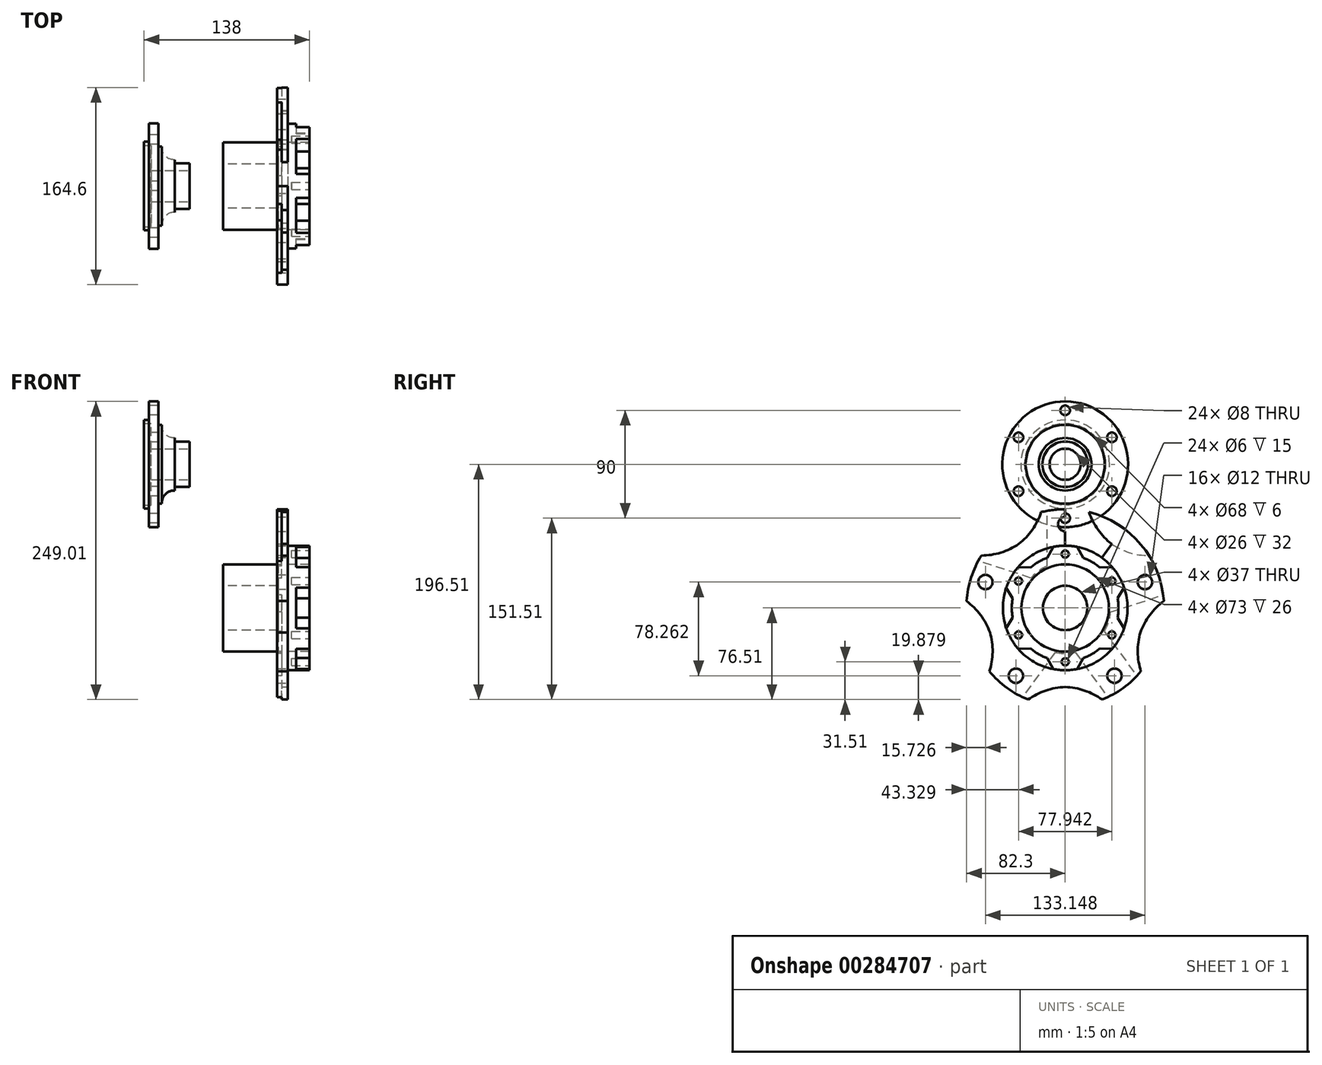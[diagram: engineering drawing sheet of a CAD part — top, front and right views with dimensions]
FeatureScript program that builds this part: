
annotation { "Feature Type Name" : "Feature", "Feature Type Description" : "" }
export const myFeature = defineFeature(function(context is Context, id is Id, definition is map)
    precondition{}
    {
        {
            var Q0;
            Q0=qCreatedBy(makeId("Front.planeOp"),FACE);
            var sketch = newSketch(context, id + "F0", { "sketchPlane" : qUnion([Q0])});
            skPoint(sketch, "E0", {"position": v(0, 13) * mm});
            skPoint(sketch, "E1", {"position": v(0, 19) * mm});
            skLineSegment(sketch, "E2", {"start": v(0, 19) * mm, "end": v(0, 13) * mm});
            skLineSegment(sketch, "E3", {"start": v(0, 19) * mm, "end": v(-12.5, 19) * mm});
            skLineSegment(sketch, "E4", {"start": v(-12.5, 19) * mm, "end": v(-12.5, 22) * mm});
            skLineSegment(sketch, "E5", {"start": v(0, 0) * mm, "end": v(-38, 0) * mm, "construction": true});
            skLineSegment(sketch, "E6", {"start": v(-38, 0) * mm, "end": v(-38, 37) * mm});
            skLineSegment(sketch, "E7", {"start": v(-38, 37) * mm, "end": v(-34, 37) * mm});
            skLineSegment(sketch, "E8", {"start": v(-34, 37) * mm, "end": v(-34, 52.5) * mm});
            skLineSegment(sketch, "E9", {"start": v(-34, 52.5) * mm, "end": v(-26, 52.5) * mm});
            skLineSegment(sketch, "E10", {"start": v(-26, 52.5) * mm, "end": v(-26, 33) * mm});
            skLineSegment(sketch, "E11", {"start": v(-26, 33) * mm, "end": v(-23, 33) * mm});
            skLineSegment(sketch, "E12", {"start": v(-23, 33) * mm, "end": v(-12.5, 33) * mm, "construction": true});
            skLineSegment(sketch, "E13", {"start": v(-12.5, 33) * mm, "end": v(-12.5, 22) * mm, "construction": true});
            skArc(sketch, "E14", {"start": v(-23, 33) * mm, "mid": v(-20.29, 25.08) * mm, "end": v(-12.5, 22) * mm});
            skLineSegment(sketch, "E15", {"start": v(-34, 37) * mm, "end": v(-32, 37) * mm});
            skLineSegment(sketch, "E16", {"start": v(-32, 37) * mm, "end": v(-32, 34) * mm});
            skLineSegment(sketch, "E17", {"start": v(-32, 34) * mm, "end": v(-38, 34) * mm});
            skLineSegment(sketch, "E18", {"start": v(-32, 34) * mm, "end": v(-32, 13) * mm});
            skLineSegment(sketch, "E19", {"start": v(-32, 13) * mm, "end": v(0, 13) * mm});
            skSolve(sketch);
        }
        {
            var Q0;
            Q0=qSketchRegion(id+"F0",true);
            var Q1;
            Q1=sQuery(id+"F0.wireOp",EDGE,"E5");
            revolve(context, id + "F1", {"entities" : qUnion([Q0]), "axis" : qUnion([Q1]), "revolveType" : RevolveType.FULL});
        }
        {
            var Q0;
            Q0=makeQuery(id+"F1.opRevolve","SWEPT_FACE",FACE,{"disambiguationData":[OSD([sQuery(id+"F0.wireOp",EDGE,"E8")])]});
            var sketch = newSketch(context, id + "F2", { "sketchPlane" : qUnion([Q0])});
            skPoint(sketch, "E20", {"position": v(0, 45) * mm});
            skCircle(sketch, "E21", {"center": v(0, 45) * mm, "radius": 4 * mm});
            skCircle(sketch, "E22.1.0", {"center": v(-38.97, 22.5) * mm, "radius": 4 * mm});
            skCircle(sketch, "E22.2.0", {"center": v(-38.97, -22.5) * mm, "radius": 4 * mm});
            skCircle(sketch, "E22.3.0", {"center": v(0, -45) * mm, "radius": 4 * mm});
            skCircle(sketch, "E22.4.0", {"center": v(38.97, -22.5) * mm, "radius": 4 * mm});
            skCircle(sketch, "E22.5.0", {"center": v(38.97, 22.5) * mm, "radius": 4 * mm});
            skPoint(sketch, "E22.center", {"position": v(0, 0) * mm});
            skSolve(sketch);
        }
        {
            var Q0;
            Q0=qSketchRegion(id+"F2",true);
            extrude(context, id + "F3", {"entities" : qUnion([Q0]), "operationType" : NewBodyOperationType.REMOVE, "oppositeDirection" : true, "depth" : 8 * mm});
        }
        {
            var Q0;
            Q0=qCreatedBy(makeId("Front.planeOp"),FACE);
            var sketch = newSketch(context, id + "F4", { "sketchPlane" : qUnion([Q0])});
            skPoint(sketch, "E23", {"position": v(0, 0) * mm});
            skPoint(sketch, "E24", {"position": v(0, -120) * mm});
            skLineSegment(sketch, "E25", {"start": v(0, -120) * mm, "end": v(100, -120) * mm, "construction": true});
            skLineSegment(sketch, "E26", {"start": v(100, -120) * mm, "end": v(100, -68) * mm, "construction": true});
            skLineSegment(sketch, "E27", {"start": v(100, -68) * mm, "end": v(82, -68) * mm});
            skLineSegment(sketch, "E28", {"start": v(82, -68) * mm, "end": v(82, -37.5) * mm});
            skLineSegment(sketch, "E29", {"start": v(82, -37.5) * mm, "end": v(73, -37.5) * mm});
            skLineSegment(sketch, "E30", {"start": v(73, -37.5) * mm, "end": v(73, -83.5) * mm});
            skLineSegment(sketch, "E31", {"start": v(73, -83.5) * mm, "end": v(28, -83.5) * mm});
            skLineSegment(sketch, "E32", {"start": v(28, -83.5) * mm, "end": v(28, -101.5) * mm});
            skLineSegment(sketch, "E33", {"start": v(28, -101.5) * mm, "end": v(73, -101.5) * mm});
            skLineSegment(sketch, "E34", {"start": v(100, -68) * mm, "end": v(100, -83.5) * mm});
            skLineSegment(sketch, "E35", {"start": v(100, -83.5) * mm, "end": v(73, -83.5) * mm});
            skLineSegment(sketch, "E36", {"start": v(73, -83.5) * mm, "end": v(73, -101.5) * mm});
            skPoint(sketch, "E37", {"position": v(73, -37.5) * mm});
            skLineSegment(sketch, "E38", {"start": v(73, -83.5) * mm, "end": v(74, -83.5) * mm});
            skLineSegment(sketch, "E39", {"start": v(74, -83.5) * mm, "end": v(74, -101.5) * mm});
            skLineSegment(sketch, "E40", {"start": v(74, -101.5) * mm, "end": v(73, -101.5) * mm});
            skSolve(sketch);
        }
        {
            var Q0;
            Q0=qSketchRegion(id+"F4",true);
            var Q1;
            Q1=makeQuery(id+"F4.imprint","IMPRINT",FACE,{"disambiguationData":[TD([[makeQuery(id+"F4.imprint","IMPRINT",EDGE,{"derivedFrom":sQuery(id+"F4.wireOp",EDGE,"E36")}),1.0]])]});
            var Q2;
            Q2=sQuery(id+"F4.wireOp",EDGE,"E25");
            revolve(context, id + "F5", {"entities" : qUnion([Q0, Q1]), "axis" : qUnion([Q2]), "revolveType" : RevolveType.FULL});
        }
        {
            var Q0;
            Q0=makeQuery(id+"F5.opRevolve","SWEPT_FACE",FACE,{"disambiguationData":[OSD([sQuery(id+"F4.wireOp",EDGE,"E28")])]});
            var sketch = newSketch(context, id + "F6", { "sketchPlane" : qUnion([Q0])});
            skCircle(sketch, "E41.0", {"center": v(0, -120) * mm, "radius": 82.5 * mm});
            skPoint(sketch, "E42", {"position": v(0, -50) * mm});
            skCircle(sketch, "E43", {"center": v(0, -50) * mm, "radius": 6 * mm});
            skCircle(sketch, "E44.1.0", {"center": v(-66.57, -98.37) * mm, "radius": 6 * mm});
            skCircle(sketch, "E44.2.0", {"center": v(-41.14, -176.63) * mm, "radius": 6 * mm});
            skCircle(sketch, "E44.3.0", {"center": v(41.14, -176.63) * mm, "radius": 6 * mm});
            skCircle(sketch, "E44.4.0", {"center": v(66.57, -98.37) * mm, "radius": 6 * mm});
            skSolve(sketch);
        }
        {
            var Q0;
            Q0=makeQuery(id+"F6.imprint","IMPRINT",FACE,{"disambiguationData":[TD([[makeQuery(id+"F6.imprint","IMPRINT",EDGE,{"derivedFrom":sQuery(id+"F6.wireOp",EDGE,"E43")}),1.0]])]});
            var Q1;
            Q1=makeQuery(id+"F6.imprint","IMPRINT",FACE,{"disambiguationData":[TD([[makeQuery(id+"F6.imprint","IMPRINT",EDGE,{"derivedFrom":sQuery(id+"F6.wireOp",EDGE,"E44.4.0")}),1.0]])]});
            var Q2;
            Q2=makeQuery(id+"F6.imprint","IMPRINT",FACE,{"disambiguationData":[TD([[makeQuery(id+"F6.imprint","IMPRINT",EDGE,{"derivedFrom":sQuery(id+"F6.wireOp",EDGE,"E44.3.0")}),1.0]])]});
            var Q3;
            Q3=makeQuery(id+"F6.imprint","IMPRINT",FACE,{"disambiguationData":[TD([[makeQuery(id+"F6.imprint","IMPRINT",EDGE,{"derivedFrom":sQuery(id+"F6.wireOp",EDGE,"E44.2.0")}),1.0]])]});
            var Q4;
            Q4=makeQuery(id+"F6.imprint","IMPRINT",FACE,{"disambiguationData":[TD([[makeQuery(id+"F6.imprint","IMPRINT",EDGE,{"derivedFrom":sQuery(id+"F6.wireOp",EDGE,"E44.1.0")}),1.0]])]});
            extrude(context, id + "F7", {"entities" : qUnion([Q0, Q1, Q2, Q3, Q4]), "operationType" : NewBodyOperationType.REMOVE, "oppositeDirection" : true, "depth" : 9 * mm});
        }
        {
            var Q0;
            Q0=makeQuery(id+"F5.opRevolve","SWEPT_FACE",FACE,{"disambiguationData":[OSD([sQuery(id+"F4.wireOp",EDGE,"E28")])]});
            var sketch = newSketch(context, id + "F8", { "sketchPlane" : qUnion([Q0])});
            skArc(sketch, "E45.0", {"start": v(-71.23, -78.37) * mm, "mid": v(-76.08, -88.1) * mm, "end": v(-79.61, -98.37) * mm});
            skLineSegment(sketch, "E46", {"start": v(0, -120) * mm, "end": v(0, -37.5) * mm});
            skCircle(sketch, "E47.0", {"center": v(-66.57, -98.37) * mm, "radius": 6 * mm});
            skLineSegment(sketch, "E48", {"start": v(0, -120) * mm, "end": v(38.8, -66.6) * mm});
            skLineSegment(sketch, "E49", {"start": v(0, -120) * mm, "end": v(-38.8, -66.6) * mm});
            skLineSegment(sketch, "E50", {"start": v(-79.61, -98.37) * mm, "end": v(-79.61, -78.37) * mm, "construction": true});
            skLineSegment(sketch, "E51", {"start": v(-79.61, -78.37) * mm, "end": v(-71.23, -78.37) * mm, "construction": true});
            skLineSegment(sketch, "E52", {"start": v(-79.61, -98.37) * mm, "end": v(-66.57, -98.37) * mm});
            skLineSegment(sketch, "E53", {"start": v(0, -37.5) * mm, "end": v(-20, -37.5) * mm, "construction": true});
            skLineSegment(sketch, "E54", {"start": v(-20, -37.5) * mm, "end": v(-20, -39.96) * mm, "construction": true});
            skArc(sketch, "E55", {"start": v(-38.8, -66.6) * mm, "mid": v(-27.41, -54.68) * mm, "end": v(-20, -39.96) * mm});
            skArc(sketch, "E56.trimOffspring", {"start": v(0, -37.5) * mm, "mid": v(-10.08, -38.12) * mm, "end": v(-20, -39.96) * mm});
            skPoint(sketch, "E57.orphan", {"position": v(79.61, -98.37) * mm});
            skArc(sketch, "E58.MirrorCS", {"start": v(0, -37.5) * mm, "mid": v(10.08, -38.12) * mm, "end": v(20, -39.96) * mm});
            skArc(sketch, "E59.MirrorCS", {"start": v(38.8, -66.6) * mm, "mid": v(27.41, -54.68) * mm, "end": v(20, -39.96) * mm});
            skArc(sketch, "E60.1.0", {"start": v(-62.77, -140.4) * mm, "mid": v(-70.6, -125.89) * mm, "end": v(-82.3, -114.29) * mm});
            skArc(sketch, "E60.1.1", {"start": v(-78.46, -94.5) * mm, "mid": v(-80.99, -104.28) * mm, "end": v(-82.3, -114.29) * mm});
            skArc(sketch, "E60.1.2", {"start": v(-78.46, -94.5) * mm, "mid": v(-74.76, -85.11) * mm, "end": v(-69.94, -76.25) * mm});
            skArc(sketch, "E60.1.3", {"start": v(-38.8, -66.6) * mm, "mid": v(-53.65, -73.74) * mm, "end": v(-69.94, -76.25) * mm});
            skLineSegment(sketch, "E60.1.5", {"start": v(0, -120) * mm, "end": v(-62.77, -140.4) * mm});
            skArc(sketch, "E60.2.0", {"start": v(0, -186) * mm, "mid": v(-16.21, -188.96) * mm, "end": v(-30.87, -196.5) * mm});
            skArc(sketch, "E60.2.1", {"start": v(-48.5, -186.74) * mm, "mid": v(-39.98, -192.17) * mm, "end": v(-30.87, -196.5) * mm});
            skArc(sketch, "E60.2.2", {"start": v(-48.5, -186.74) * mm, "mid": v(-56.28, -180.32) * mm, "end": v(-63.23, -173) * mm});
            skArc(sketch, "E60.2.3", {"start": v(-62.77, -140.4) * mm, "mid": v(-60.57, -156.73) * mm, "end": v(-63.23, -173) * mm});
            skLineSegment(sketch, "E60.2.4", {"start": v(0, -120) * mm, "end": v(-62.77, -140.4) * mm});
            skLineSegment(sketch, "E60.2.5", {"start": v(0, -120) * mm, "end": v(0, -186) * mm});
            skArc(sketch, "E60.3.0", {"start": v(62.77, -140.4) * mm, "mid": v(60.57, -156.73) * mm, "end": v(63.23, -173) * mm});
            skArc(sketch, "E60.3.1", {"start": v(48.5, -186.74) * mm, "mid": v(56.28, -180.32) * mm, "end": v(63.23, -173) * mm});
            skArc(sketch, "E60.3.2", {"start": v(48.5, -186.74) * mm, "mid": v(39.98, -192.17) * mm, "end": v(30.87, -196.5) * mm});
            skArc(sketch, "E60.3.3", {"start": v(0, -186) * mm, "mid": v(16.21, -188.96) * mm, "end": v(30.87, -196.5) * mm});
            skLineSegment(sketch, "E60.3.4", {"start": v(0, -120) * mm, "end": v(0, -186) * mm});
            skLineSegment(sketch, "E60.3.5", {"start": v(0, -120) * mm, "end": v(62.77, -140.4) * mm});
            skArc(sketch, "E60.4.0", {"start": v(38.8, -66.6) * mm, "mid": v(53.65, -73.74) * mm, "end": v(69.94, -76.25) * mm});
            skArc(sketch, "E60.4.1", {"start": v(78.46, -94.5) * mm, "mid": v(74.76, -85.11) * mm, "end": v(69.94, -76.25) * mm});
            skArc(sketch, "E60.4.2", {"start": v(78.46, -94.5) * mm, "mid": v(80.99, -104.28) * mm, "end": v(82.3, -114.29) * mm});
            skArc(sketch, "E60.4.3", {"start": v(62.77, -140.4) * mm, "mid": v(70.6, -125.89) * mm, "end": v(82.3, -114.29) * mm});
            skLineSegment(sketch, "E60.4.4", {"start": v(0, -120) * mm, "end": v(62.77, -140.4) * mm});
            skCircle(sketch, "E61.0", {"center": v(0, -120) * mm, "radius": 82.5 * mm});
            skSolve(sketch);
        }
        {
            var Q0;
            {var subQ0=sQuery(id+"F8.wireOp",EDGE,"E55");Q0=makeQuery(id+"F8.imprint","IMPRINT",FACE,{"disambiguationData":[TD([[makeQuery(id+"F8.imprint","IMPRINT",EDGE,{"derivedFrom":subQ0}),1.0]])]});}
            var Q1;
            {var subQ0=sQuery(id+"F8.wireOp",EDGE,"E59.MirrorCS");Q1=makeQuery(id+"F8.imprint","IMPRINT",FACE,{"disambiguationData":[TD([[makeQuery(id+"F8.imprint","IMPRINT",EDGE,{"derivedFrom":subQ0}),-1.0]])]});}
            var Q2;
            {var subQ0=sQuery(id+"F8.wireOp",EDGE,"E60.3.0");Q2=makeQuery(id+"F8.imprint","IMPRINT",FACE,{"disambiguationData":[TD([[makeQuery(id+"F8.imprint","IMPRINT",EDGE,{"derivedFrom":subQ0}),1.0]])]});}
            var Q3;
            {var subQ0=sQuery(id+"F8.wireOp",EDGE,"E60.2.0");Q3=makeQuery(id+"F8.imprint","IMPRINT",FACE,{"disambiguationData":[TD([[makeQuery(id+"F8.imprint","IMPRINT",EDGE,{"derivedFrom":subQ0}),1.0]])]});}
            var Q4;
            {var subQ0=sQuery(id+"F8.wireOp",EDGE,"E60.1.0");Q4=makeQuery(id+"F8.imprint","IMPRINT",FACE,{"disambiguationData":[TD([[makeQuery(id+"F8.imprint","IMPRINT",EDGE,{"derivedFrom":subQ0}),1.0]])]});}
            extrude(context, id + "F9", {"entities" : qUnion([Q0, Q1, Q2, Q3, Q4]), "operationType" : NewBodyOperationType.REMOVE, "oppositeDirection" : true, "depth" : 9 * mm});
        }
        {
            var Q0;
            Q0=makeQuery(id+"F5.opRevolve","SWEPT_FACE",FACE,{"disambiguationData":[OSD([sQuery(id+"F4.wireOp",EDGE,"E34")])]});
            var sketch = newSketch(context, id + "F10", { "sketchPlane" : qUnion([Q0])});
            skCircle(sketch, "E62.0", {"center": v(0, -120) * mm, "radius": 36.5 * mm});
            skPoint(sketch, "E63", {"position": v(0, -75) * mm});
            skCircle(sketch, "E64", {"center": v(0, -75) * mm, "radius": 3 * mm});
            skCircle(sketch, "E65.1.0", {"center": v(-38.97, -97.5) * mm, "radius": 3 * mm});
            skCircle(sketch, "E65.2.0", {"center": v(-38.97, -142.5) * mm, "radius": 3 * mm});
            skCircle(sketch, "E65.3.0", {"center": v(0, -165) * mm, "radius": 3 * mm});
            skCircle(sketch, "E65.4.0", {"center": v(38.97, -142.5) * mm, "radius": 3 * mm});
            skCircle(sketch, "E65.5.0", {"center": v(38.97, -97.5) * mm, "radius": 3 * mm});
            skSolve(sketch);
        }
        {
            var Q0;
            Q0=makeQuery(id+"F10.imprint","IMPRINT",FACE,{"disambiguationData":[TD([[makeQuery(id+"F10.imprint","IMPRINT",EDGE,{"derivedFrom":sQuery(id+"F10.wireOp",EDGE,"E64")}),1.0]])]});
            var Q1;
            Q1=makeQuery(id+"F10.imprint","IMPRINT",FACE,{"disambiguationData":[TD([[makeQuery(id+"F10.imprint","IMPRINT",EDGE,{"derivedFrom":sQuery(id+"F10.wireOp",EDGE,"E65.1.0")}),1.0]])]});
            var Q2;
            Q2=makeQuery(id+"F10.imprint","IMPRINT",FACE,{"disambiguationData":[TD([[makeQuery(id+"F10.imprint","IMPRINT",EDGE,{"derivedFrom":sQuery(id+"F10.wireOp",EDGE,"E65.2.0")}),1.0]])]});
            var Q3;
            Q3=makeQuery(id+"F10.imprint","IMPRINT",FACE,{"disambiguationData":[TD([[makeQuery(id+"F10.imprint","IMPRINT",EDGE,{"derivedFrom":sQuery(id+"F10.wireOp",EDGE,"E65.3.0")}),1.0]])]});
            var Q4;
            Q4=makeQuery(id+"F10.imprint","IMPRINT",FACE,{"disambiguationData":[TD([[makeQuery(id+"F10.imprint","IMPRINT",EDGE,{"derivedFrom":sQuery(id+"F10.wireOp",EDGE,"E65.4.0")}),1.0]])]});
            var Q5;
            Q5=makeQuery(id+"F10.imprint","IMPRINT",FACE,{"disambiguationData":[TD([[makeQuery(id+"F10.imprint","IMPRINT",EDGE,{"derivedFrom":sQuery(id+"F10.wireOp",EDGE,"E65.5.0")}),1.0]])]});
            extrude(context, id + "F11", {"entities" : qUnion([Q0, Q1, Q2, Q3, Q4, Q5]), "operationType" : NewBodyOperationType.REMOVE, "oppositeDirection" : true, "depth" : 15 * mm});
        }
        {
            var Q0;
            Q0=makeQuery(id+"F5.opRevolve","SWEPT_FACE",FACE,{"disambiguationData":[OSD([sQuery(id+"F4.wireOp",EDGE,"E34")])]});
            var sketch = newSketch(context, id + "F12", { "sketchPlane" : qUnion([Q0])});
            skCircle(sketch, "E66.0", {"center": v(0, -120) * mm, "radius": 36.5 * mm});
            skCircle(sketch, "E67.0", {"center": v(0, -75) * mm, "radius": 3 * mm});
            skCircle(sketch, "E68.0", {"center": v(38.97, -97.5) * mm, "radius": 3 * mm});
            skCircle(sketch, "E69.0", {"center": v(38.97, -142.5) * mm, "radius": 3 * mm});
            skCircle(sketch, "E70.0", {"center": v(0, -165) * mm, "radius": 3 * mm});
            skCircle(sketch, "E71.0", {"center": v(-38.97, -142.5) * mm, "radius": 3 * mm});
            skCircle(sketch, "E72.0", {"center": v(-38.97, -97.5) * mm, "radius": 3 * mm});
            skArc(sketch, "E73.0", {"start": v(10, -68.97) * mm, "mid": v(0, -68) * mm, "end": v(-10, -68.97) * mm});
            skPoint(sketch, "E74", {"position": v(0, -68) * mm});
            skPoint(sketch, "E75", {"position": v(10, -68) * mm});
            skPoint(sketch, "E76", {"position": v(-10, -68) * mm});
            skPoint(sketch, "E77", {"position": v(-10, -68.97) * mm});
            skPoint(sketch, "E78", {"position": v(10, -68.97) * mm});
            skPoint(sketch, "E79", {"position": v(-15, -68) * mm});
            skPoint(sketch, "E80", {"position": v(15, -68) * mm});
            skCircle(sketch, "E81", {"center": v(0, -120) * mm, "radius": 44.5 * mm});
            skPoint(sketch, "E82", {"position": v(-15, -78.1) * mm});
            skPoint(sketch, "E83", {"position": v(15, -78.1) * mm});
            skLineSegment(sketch, "E84", {"start": v(-10, -68.97) * mm, "end": v(-15, -78.1) * mm});
            skLineSegment(sketch, "E85", {"start": v(10, -68.97) * mm, "end": v(15, -78.1) * mm});
            skArc(sketch, "E86.1.0", {"start": v(-39.2, -85.83) * mm, "mid": v(-45.03, -94) * mm, "end": v(-49.2, -103.15) * mm});
            skPoint(sketch, "E86.1.1", {"position": v(-39.2, -85.83) * mm});
            skLineSegment(sketch, "E86.1.2", {"start": v(-39.2, -85.83) * mm, "end": v(-28.78, -86.06) * mm});
            skLineSegment(sketch, "E86.1.4", {"start": v(-49.2, -103.15) * mm, "end": v(-43.78, -112.04) * mm});
            skArc(sketch, "E86.2.0", {"start": v(-49.2, -136.85) * mm, "mid": v(-45.03, -146) * mm, "end": v(-39.2, -154.17) * mm});
            skPoint(sketch, "E86.2.1", {"position": v(-49.2, -136.85) * mm});
            skLineSegment(sketch, "E86.2.2", {"start": v(-49.2, -136.85) * mm, "end": v(-43.78, -127.96) * mm});
            skLineSegment(sketch, "E86.2.4", {"start": v(-39.2, -154.17) * mm, "end": v(-28.78, -153.94) * mm});
            skArc(sketch, "E86.3.0", {"start": v(-10, -171.03) * mm, "mid": v(0, -172) * mm, "end": v(10, -171.03) * mm});
            skPoint(sketch, "E86.3.1", {"position": v(-10, -171.03) * mm});
            skLineSegment(sketch, "E86.3.2", {"start": v(-10, -171.03) * mm, "end": v(-15, -161.9) * mm});
            skLineSegment(sketch, "E86.3.4", {"start": v(10, -171.03) * mm, "end": v(15, -161.9) * mm});
            skArc(sketch, "E86.4.0", {"start": v(39.2, -154.17) * mm, "mid": v(45.03, -146) * mm, "end": v(49.2, -136.85) * mm});
            skPoint(sketch, "E86.4.1", {"position": v(39.2, -154.17) * mm});
            skLineSegment(sketch, "E86.4.2", {"start": v(39.2, -154.17) * mm, "end": v(28.78, -153.94) * mm});
            skLineSegment(sketch, "E86.4.4", {"start": v(49.2, -136.85) * mm, "end": v(43.78, -127.96) * mm});
            skArc(sketch, "E86.5.0", {"start": v(49.2, -103.15) * mm, "mid": v(45.03, -94) * mm, "end": v(39.2, -85.83) * mm});
            skPoint(sketch, "E86.5.1", {"position": v(49.2, -103.15) * mm});
            skLineSegment(sketch, "E86.5.2", {"start": v(49.2, -103.15) * mm, "end": v(43.78, -112.04) * mm});
            skLineSegment(sketch, "E86.5.4", {"start": v(39.2, -85.83) * mm, "end": v(28.78, -86.06) * mm});
            skCircle(sketch, "E87.0", {"center": v(0, -120) * mm, "radius": 52 * mm});
            skSolve(sketch);
        }
        {
            var Q0;
            {var subQ0=sQuery(id+"F12.wireOp",EDGE,"E86.4.4");Q0=makeQuery(id+"F12.imprint","IMPRINT",FACE,{"disambiguationData":[TD([[makeQuery(id+"F12.imprint","IMPRINT",EDGE,{"derivedFrom":subQ0}),-1.0]])]});}
            var Q1;
            {var subQ0=sQuery(id+"F12.wireOp",EDGE,"E84");Q1=makeQuery(id+"F12.imprint","IMPRINT",FACE,{"disambiguationData":[TD([[makeQuery(id+"F12.imprint","IMPRINT",EDGE,{"derivedFrom":subQ0}),-1.0]])]});}
            var Q2;
            {var subQ0=sQuery(id+"F12.wireOp",EDGE,"E85");Q2=makeQuery(id+"F12.imprint","IMPRINT",FACE,{"disambiguationData":[TD([[makeQuery(id+"F12.imprint","IMPRINT",EDGE,{"derivedFrom":subQ0}),1.0]])]});}
            var Q3;
            {var subQ0=sQuery(id+"F12.wireOp",EDGE,"E86.1.4");Q3=makeQuery(id+"F12.imprint","IMPRINT",FACE,{"disambiguationData":[TD([[makeQuery(id+"F12.imprint","IMPRINT",EDGE,{"derivedFrom":subQ0}),-1.0]])]});}
            var Q4;
            {var subQ0=sQuery(id+"F12.wireOp",EDGE,"E86.2.4");Q4=makeQuery(id+"F12.imprint","IMPRINT",FACE,{"disambiguationData":[TD([[makeQuery(id+"F12.imprint","IMPRINT",EDGE,{"derivedFrom":subQ0}),-1.0]])]});}
            var Q5;
            {var subQ0=sQuery(id+"F12.wireOp",EDGE,"E86.3.4");Q5=makeQuery(id+"F12.imprint","IMPRINT",FACE,{"disambiguationData":[TD([[makeQuery(id+"F12.imprint","IMPRINT",EDGE,{"derivedFrom":subQ0}),-1.0]])]});}
            extrude(context, id + "F13", {"entities" : qUnion([Q0, Q1, Q2, Q3, Q4, Q5]), "operationType" : NewBodyOperationType.REMOVE, "oppositeDirection" : true, "depth" : 11 * mm});
        }
        {
            var Q0;
            Q0=makeQuery(id+"F5.opRevolve","SWEPT_FACE",FACE,{"disambiguationData":[OSD([sQuery(id+"F4.wireOp",EDGE,"E30")])]});
            var sketch = newSketch(context, id + "F14", { "sketchPlane" : qUnion([Q0])});
            skCircle(sketch, "E88.0", {"center": v(0, -120) * mm, "radius": 18.5 * mm});
            skPoint(sketch, "E89", {"position": v(0, -81) * mm});
            skPoint(sketch, "E90", {"position": v(15, -81) * mm});
            skPoint(sketch, "E91", {"position": v(-15, -81) * mm});
            skPoint(sketch, "E92", {"position": v(-15, -86.72) * mm});
            skPoint(sketch, "E93", {"position": v(99.52, -81) * mm});
            skPoint(sketch, "E94", {"position": v(15, -86.72) * mm});
            skArc(sketch, "E95.0", {"start": v(15, -86.72) * mm, "mid": v(0, -83.5) * mm, "end": v(-15, -86.72) * mm});
            skLineSegment(sketch, "E96", {"start": v(-15, -86.72) * mm, "end": v(-15, -38.88) * mm});
            skLineSegment(sketch, "E97", {"start": v(15, -86.72) * mm, "end": v(15, -38.88) * mm});
            skArc(sketch, "E98.0", {"start": v(15, -38.88) * mm, "mid": v(0, -37.5) * mm, "end": v(-15, -38.88) * mm});
            skPoint(sketch, "E99.orphan", {"position": v(20, -39.96) * mm});
            skPoint(sketch, "E100.orphan", {"position": v(-20, -39.96) * mm});
            skLineSegment(sketch, "E101.1.0", {"start": v(-36.28, -123.98) * mm, "end": v(-81.79, -109.2) * mm});
            skLineSegment(sketch, "E101.1.1", {"start": v(-27.01, -95.45) * mm, "end": v(-72.52, -80.67) * mm});
            skArc(sketch, "E101.1.2", {"start": v(-72.52, -80.67) * mm, "mid": v(-78.46, -94.5) * mm, "end": v(-81.79, -109.2) * mm});
            skArc(sketch, "E101.1.3", {"start": v(-27.01, -95.45) * mm, "mid": v(-34.71, -108.72) * mm, "end": v(-36.28, -123.98) * mm});
            skLineSegment(sketch, "E101.2.0", {"start": v(-7.42, -155.74) * mm, "end": v(-35.55, -194.45) * mm});
            skLineSegment(sketch, "E101.2.1", {"start": v(-31.7, -138.1) * mm, "end": v(-59.82, -176.81) * mm});
            skArc(sketch, "E101.2.2", {"start": v(-59.82, -176.81) * mm, "mid": v(-48.5, -186.74) * mm, "end": v(-35.55, -194.45) * mm});
            skArc(sketch, "E101.2.3", {"start": v(-31.7, -138.1) * mm, "mid": v(-21.45, -149.53) * mm, "end": v(-7.42, -155.74) * mm});
            skLineSegment(sketch, "E101.3.0", {"start": v(31.7, -138.1) * mm, "end": v(59.82, -176.81) * mm});
            skLineSegment(sketch, "E101.3.1", {"start": v(7.42, -155.74) * mm, "end": v(35.55, -194.45) * mm});
            skArc(sketch, "E101.3.2", {"start": v(35.55, -194.45) * mm, "mid": v(48.5, -186.74) * mm, "end": v(59.82, -176.81) * mm});
            skArc(sketch, "E101.3.3", {"start": v(7.42, -155.74) * mm, "mid": v(21.45, -149.53) * mm, "end": v(31.7, -138.1) * mm});
            skLineSegment(sketch, "E101.4.0", {"start": v(27.01, -95.45) * mm, "end": v(72.52, -80.67) * mm});
            skLineSegment(sketch, "E101.4.1", {"start": v(36.28, -123.98) * mm, "end": v(81.79, -109.2) * mm});
            skArc(sketch, "E101.4.2", {"start": v(81.79, -109.2) * mm, "mid": v(78.46, -94.5) * mm, "end": v(72.52, -80.67) * mm});
            skArc(sketch, "E101.4.3", {"start": v(36.28, -123.98) * mm, "mid": v(34.71, -108.72) * mm, "end": v(27.01, -95.45) * mm});
            skArc(sketch, "E102.0", {"start": v(-38.8, -66.6) * mm, "mid": v(-53.65, -73.74) * mm, "end": v(-69.94, -76.25) * mm});
            skArc(sketch, "E103.0", {"start": v(-38.8, -66.6) * mm, "mid": v(-27.41, -54.68) * mm, "end": v(-20, -39.96) * mm});
            skArc(sketch, "E104.0", {"start": v(38.8, -66.6) * mm, "mid": v(27.41, -54.68) * mm, "end": v(20, -39.96) * mm});
            skArc(sketch, "E105.0", {"start": v(20, -39.96) * mm, "mid": v(0, -37.5) * mm, "end": v(-20, -39.96) * mm});
            skArc(sketch, "E106.0", {"start": v(38.8, -66.6) * mm, "mid": v(53.65, -73.74) * mm, "end": v(69.94, -76.25) * mm});
            skArc(sketch, "E107.0", {"start": v(82.3, -114.29) * mm, "mid": v(78.46, -94.5) * mm, "end": v(69.94, -76.25) * mm});
            skArc(sketch, "E108.0", {"start": v(62.77, -140.4) * mm, "mid": v(60.57, -156.73) * mm, "end": v(63.23, -173) * mm});
            skArc(sketch, "E109.0", {"start": v(62.77, -140.4) * mm, "mid": v(70.6, -125.89) * mm, "end": v(82.3, -114.29) * mm});
            skArc(sketch, "E110.0", {"start": v(0, -186) * mm, "mid": v(16.21, -188.96) * mm, "end": v(30.87, -196.5) * mm});
            skArc(sketch, "E111.0", {"start": v(0, -186) * mm, "mid": v(-16.21, -188.96) * mm, "end": v(-30.87, -196.5) * mm});
            skArc(sketch, "E112.0", {"start": v(-63.23, -173) * mm, "mid": v(-48.5, -186.74) * mm, "end": v(-30.87, -196.5) * mm});
            skArc(sketch, "E113.0", {"start": v(-62.77, -140.4) * mm, "mid": v(-60.57, -156.73) * mm, "end": v(-63.23, -173) * mm});
            skArc(sketch, "E114.0", {"start": v(-62.77, -140.4) * mm, "mid": v(-70.6, -125.89) * mm, "end": v(-82.3, -114.29) * mm});
            skArc(sketch, "E115.0", {"start": v(-69.94, -76.25) * mm, "mid": v(-78.46, -94.5) * mm, "end": v(-82.3, -114.29) * mm});
            skCircle(sketch, "E116.0", {"center": v(0, -120) * mm, "radius": 36.5 * mm});
            skCircle(sketch, "E117", {"center": v(0, -120) * mm, "radius": 38 * mm});
            skSolve(sketch);
        }
        {
            var Q0;
            {var subQ2=sQuery(id+"F14.wireOp",EDGE,"E102.0");Q0=makeQuery(id+"F14.imprint","IMPRINT",FACE,{"disambiguationData":[TD([[makeQuery(id+"F14.imprint","IMPRINT",EDGE,{"derivedFrom":subQ2}),1.0]])]});}
            var Q1;
            {var subQ0=sQuery(id+"F14.wireOp",EDGE,"E113.0");Q1=makeQuery(id+"F14.imprint","IMPRINT",FACE,{"disambiguationData":[TD([[makeQuery(id+"F14.imprint","IMPRINT",EDGE,{"derivedFrom":subQ0}),1.0]])]});}
            var Q2;
            {var subQ12=sQuery(id+"F14.wireOp",EDGE,"E110.0");Q2=makeQuery(id+"F14.imprint","IMPRINT",FACE,{"disambiguationData":[TD([[makeQuery(id+"F14.imprint","IMPRINT",EDGE,{"derivedFrom":subQ12}),1.0]])]});}
            var Q3;
            {var subQ0=sQuery(id+"F14.wireOp",EDGE,"E108.0");Q3=makeQuery(id+"F14.imprint","IMPRINT",FACE,{"disambiguationData":[TD([[makeQuery(id+"F14.imprint","IMPRINT",EDGE,{"derivedFrom":subQ0}),-1.0]])]});}
            var Q4;
            {var subQ1=sQuery(id+"F14.wireOp",EDGE,"E104.0");Q4=makeQuery(id+"F14.imprint","IMPRINT",FACE,{"disambiguationData":[TD([[makeQuery(id+"F14.imprint","IMPRINT",EDGE,{"derivedFrom":subQ1}),1.0]])]});}
            extrude(context, id + "F15", {"entities" : qUnion([Q0, Q1, Q2, Q3, Q4]), "operationType" : NewBodyOperationType.REMOVE, "oppositeDirection" : true, "depth" : 4 * mm});
        }
    });
